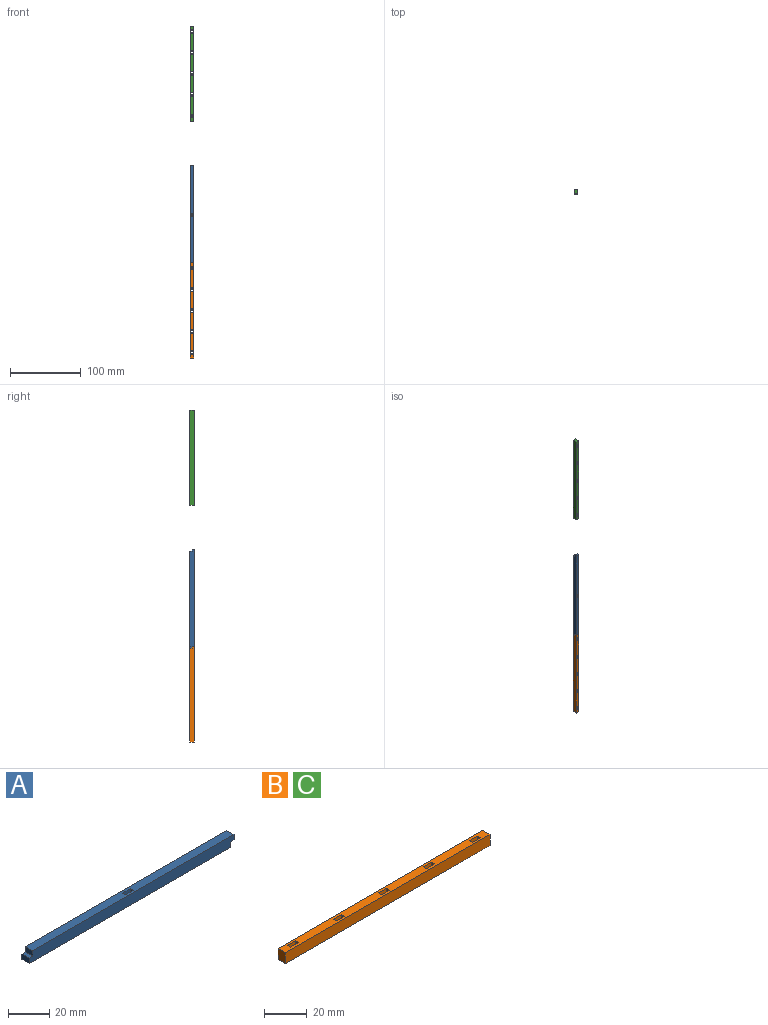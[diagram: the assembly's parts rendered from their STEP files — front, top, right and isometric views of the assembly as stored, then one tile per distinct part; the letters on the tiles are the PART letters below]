
ASSEMBLY  parts=3 mates=1
PART A: 14 faces, bbox 140x4.9x6.3 mm
  f0: plane 4.85x3.13mm, normal (-1,0,0), area 15.2mm2, adj f3,f4,f5,f12
  f1: plane 4.85x3.13mm, normal (1,0,0), area 15.2mm2, adj f2,f4,f5,f10
  f2: plane 137.5x4.85mm, normal (0,0,1), area 656mm2, adj f1,f4,f5,f6,f7,f8,f9,f13
  f3: plane 137.5x4.85mm, normal (0,0,-1), area 656mm2, adj f0,f4,f5,f6,f7,f8,f9,f11
  f4: plane 140x6.25mm, normal (0,-1,0), area 859.4mm2, adj f0,f1,f2,f3,f10,f11,f12,f13
  f5: plane 140x6.25mm, normal (0,1,0), area 859.4mm2, adj f0,f1,f2,f3,f10,f11,f12,f13
  f6: plane 6.25x2.05mm, normal (1,0,0), area 12.8mm2, adj f2,f3,f7,f8
  f7: plane 6.25x5.3mm, normal (0,1,0), area 33.1mm2, adj f2,f3,f6,f9
  f8: plane 6.25x5.3mm, normal (0,-1,0), area 33.1mm2, adj f2,f3,f6,f9
  f9: plane 6.25x2.05mm, normal (-1,0,0), area 12.8mm2, adj f2,f3,f7,f8
  f10: plane 4.85x2.5mm, normal (0,0,-1), area 12.1mm2, adj f1,f4,f5,f11
  f11: plane 4.85x3.13mm, normal (1,0,0), area 15.2mm2, adj f3,f4,f5,f10
  f12: plane 4.85x2.5mm, normal (0,0,1), area 12.1mm2, adj f0,f4,f5,f13
  f13: plane 4.85x3.13mm, normal (-1,0,0), area 15.2mm2, adj f2,f4,f5,f12
PART B: 26 faces, bbox 135x4.9x6.3 mm
  f0: plane 6.25x5.3mm, normal (0,-1,0), area 33.1mm2, adj f1,f3,f16,f17
  f1: plane 6.25x2.05mm, normal (1,0,0), area 12.8mm2, adj f0,f2,f16,f17
  f2: plane 6.25x5.3mm, normal (0,1,0), area 33.1mm2, adj f1,f3,f16,f17
  f3: plane 6.25x2.05mm, normal (-1,0,0), area 12.8mm2, adj f0,f2,f16,f17
  f4: plane 6.25x5.3mm, normal (0,-1,0), area 33.1mm2, adj f5,f7,f16,f17
  f5: plane 6.25x2.05mm, normal (1,0,0), area 12.8mm2, adj f4,f6,f16,f17
  f6: plane 6.25x5.3mm, normal (0,1,0), area 33.1mm2, adj f5,f7,f16,f17
  f7: plane 6.25x2.05mm, normal (-1,0,0), area 12.8mm2, adj f4,f6,f16,f17
  f8: plane 6.25x5.3mm, normal (0,-1,0), area 33.1mm2, adj f9,f11,f16,f17
  f9: plane 6.25x2.05mm, normal (1,0,0), area 12.8mm2, adj f8,f10,f16,f17
  f10: plane 6.25x5.3mm, normal (0,1,0), area 33.1mm2, adj f9,f11,f16,f17
  f11: plane 6.25x2.05mm, normal (-1,0,0), area 12.8mm2, adj f8,f10,f16,f17
  f12: plane 6.25x5.3mm, normal (0,-1,0), area 33.1mm2, adj f13,f15,f16,f17
  f13: plane 6.25x2.05mm, normal (1,0,0), area 12.8mm2, adj f12,f14,f16,f17
  f14: plane 6.25x5.3mm, normal (0,1,0), area 33.1mm2, adj f13,f15,f16,f17
  f15: plane 6.25x2.05mm, normal (-1,0,0), area 12.8mm2, adj f12,f14,f16,f17
  f16: plane 135x4.85mm, normal (0,0,1), area 600.4mm2, adj f0,f1,f2,f3,f4,f5,f6,f7
  f17: plane 135x4.85mm, normal (0,0,-1), area 600.4mm2, adj f0,f1,f2,f3,f4,f5,f6,f7
  f18: plane 135x6.25mm, normal (0,-1,0), area 843.8mm2, adj f16,f17,f19,f21
  f19: plane 6.25x4.85mm, normal (1,0,0), area 30.3mm2, adj f16,f17,f18,f20
  f20: plane 135x6.25mm, normal (0,1,0), area 843.8mm2, adj f16,f17,f19,f21
  f21: plane 6.25x4.85mm, normal (-1,0,0), area 30.3mm2, adj f16,f17,f18,f20
  f22: plane 6.25x2.05mm, normal (1,0,0), area 12.8mm2, adj f16,f17,f23,f24
  f23: plane 6.25x5.3mm, normal (0,1,0), area 33.1mm2, adj f16,f17,f22,f25
  f24: plane 6.25x5.3mm, normal (0,-1,0), area 33.1mm2, adj f16,f17,f22,f25
  f25: plane 6.25x2.05mm, normal (-1,0,0), area 12.8mm2, adj f16,f17,f23,f24
PART C: same geometry as B
PLACE A rot(axis=(-0.58,0.58,0.58),120deg) t=(0,-3.13,-267.5)mm
PLACE B rot(axis=(0.58,-0.58,0.58),120deg) t=(0,3.12,-470)mm
PLACE C rot(axis=(-0.58,0.58,0.58),120deg) t=(0,-3.12,0)mm
MATE planar B.f19 <-> A.f11  axis (0,0,1) through (0,0,-335)mm
